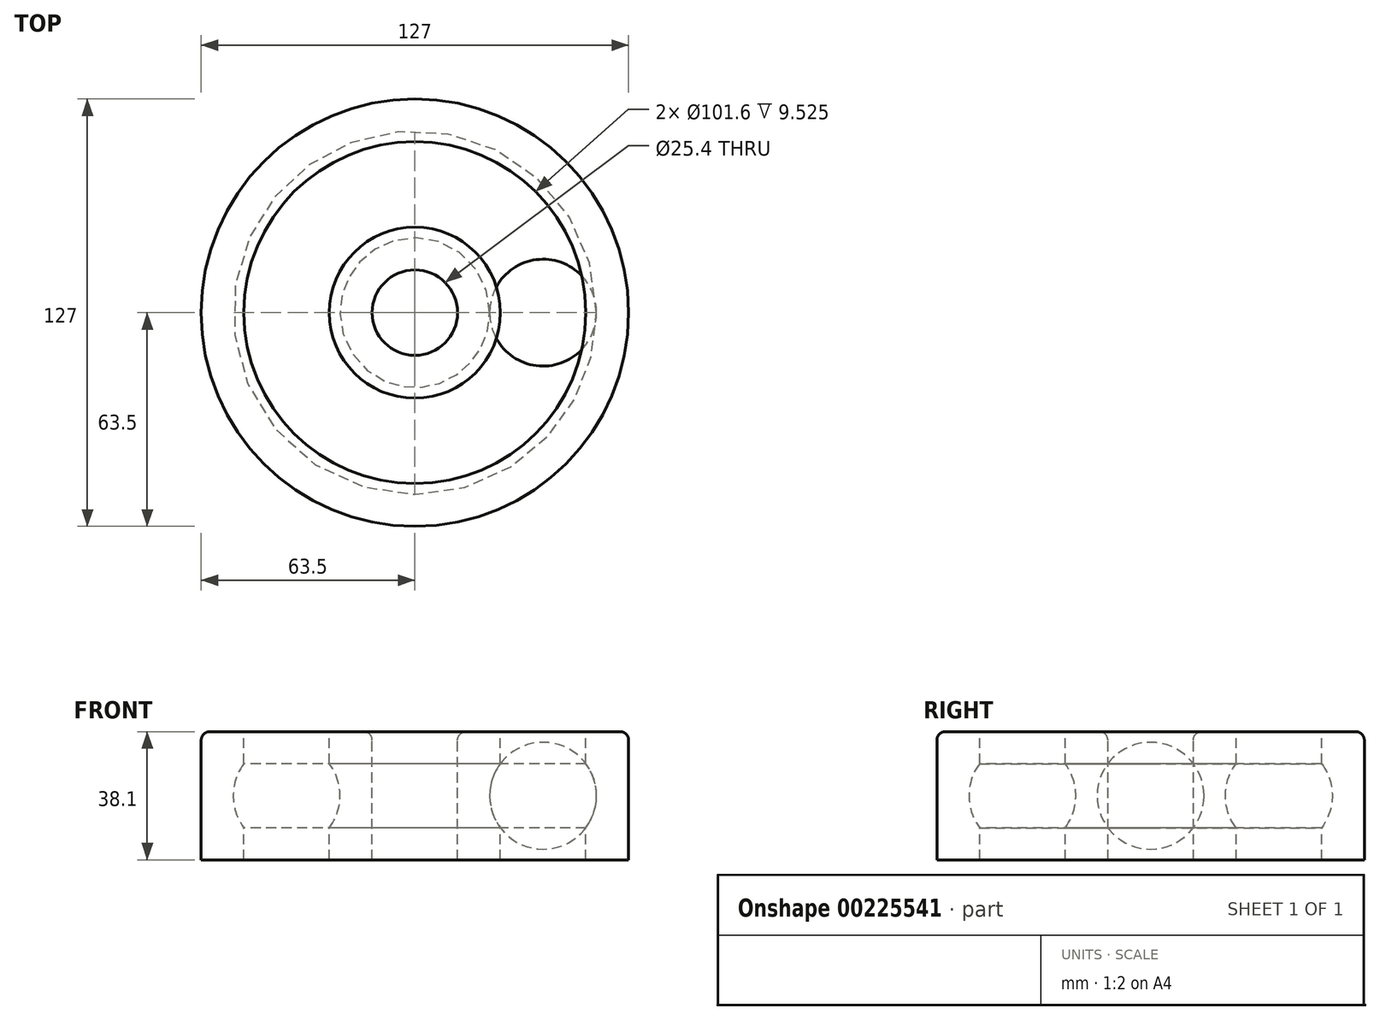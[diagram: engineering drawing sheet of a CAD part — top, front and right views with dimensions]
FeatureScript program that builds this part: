
annotation { "Feature Type Name" : "Feature", "Feature Type Description" : "" }
export const myFeature = defineFeature(function(context is Context, id is Id, definition is map)
    precondition{}
    {
        {
            var Q0;
            Q0=qCreatedBy(makeId("Front.planeOp"),FACE);
            var sketch = newSketch(context, id + "F0", { "sketchPlane" : qUnion([Q0])});
            skLineSegment(sketch, "E0", {"start": v(0, 19.05) * mm, "end": v(0, -19.05) * mm, "construction": true});
            skLineSegment(sketch, "E1", {"start": v(12.7, 19.05) * mm, "end": v(12.7, -19.05) * mm});
            skLineSegment(sketch, "E2", {"start": v(12.7, -19.05) * mm, "end": v(25.4, -19.05) * mm});
            skLineSegment(sketch, "E3", {"start": v(25.4, -19.05) * mm, "end": v(25.4, 19.05) * mm});
            skLineSegment(sketch, "E4", {"start": v(25.4, 19.05) * mm, "end": v(12.7, 19.05) * mm});
            skCircle(sketch, "E5", {"center": v(38.1, 0) * mm, "radius": 15.88 * mm});
            skLineSegment(sketch, "E6.bottom", {"start": v(50.8, 19.05) * mm, "end": v(63.5, 19.05) * mm});
            skLineSegment(sketch, "E6.top", {"start": v(50.8, -19.05) * mm, "end": v(63.5, -19.05) * mm});
            skLineSegment(sketch, "E6.left", {"start": v(50.8, 19.05) * mm, "end": v(50.8, -19.05) * mm});
            skLineSegment(sketch, "E6.right", {"start": v(63.5, 19.05) * mm, "end": v(63.5, -19.05) * mm});
            skLineSegment(sketch, "E7", {"start": v(22.22, 0) * mm, "end": v(53.97, 0) * mm});
            skLineSegment(sketch, "E8", {"start": v(12.7, 0) * mm, "end": v(22.22, 0) * mm, "construction": true});
            skLineSegment(sketch, "E9", {"start": v(53.97, 0) * mm, "end": v(63.5, 0) * mm, "construction": true});
            skSolve(sketch);
        }
        {
            var Q0;
            {var subQ6=sQuery(id+"F0.wireOp",EDGE,"E6.bottom");Q0=makeQuery(id+"F0.imprint","IMPRINT",FACE,{"disambiguationData":[TD([[makeQuery(id+"F0.imprint","IMPRINT",EDGE,{"derivedFrom":subQ6}),-1.0]])]});}
            var Q1;
            Q1=makeQuery(id+"F0.imprint","IMPRINT",FACE,{"disambiguationData":[TD([[makeQuery(id+"F0.imprint","IMPRINT",EDGE,{"derivedFrom":sQuery(id+"F0.wireOp",EDGE,"E1")}),1.0]])]});
            var Q2;
            Q2=sQuery(id+"F0.wireOp",EDGE,"E0");
            revolve(context, id + "F1", {"entities" : qUnion([Q0, Q1]), "axis" : qUnion([Q2]), "revolveType" : RevolveType.FULL});
        }
        {
            var Q0;
            Q0=qCreatedBy(makeId("Front.planeOp"),FACE);
            var sketch = newSketch(context, id + "F2", { "sketchPlane" : qUnion([Q0])});
            skCircle(sketch, "E10.0", {"center": v(38.1, 0) * mm, "radius": 15.88 * mm});
            skSolve(sketch);
        }
        {
            var Q0;
            {var subQ0=sQuery(id+"F0.wireOp",EDGE,"E5");var subQ1=sQuery(id+"F0.wireOp",EDGE,"E3");var subQ2=makeQuery(id+"F0.imprint","INTERSECT",VERTEX,{"disambiguationData":[OD(0.0)],"derivedFrom":[subQ1,subQ0]});Q0=makeQuery(id+"F0.imprint","IMPRINT",FACE,{"disambiguationData":[TD([[makeQuery(id+"F0.imprint","IMPRINT",EDGE,{"disambiguationData":[TD([[subQ2,-1.0]])],"derivedFrom":subQ1}),-1.0]])]});}
            var sketch = newSketch(context, id + "F3", { "sketchPlane" : qUnion([Q0])});
            skArc(sketch, "E11.0", {"start": v(53.97, 0) * mm, "mid": v(38.1, 15.88) * mm, "end": v(22.22, 0) * mm});
            skLineSegment(sketch, "E12.0", {"start": v(22.22, 0) * mm, "end": v(53.97, 0) * mm});
            skLineSegment(sketch, "E13.1", {"start": v(12.7, 0) * mm, "end": v(22.22, 0) * mm});
            skLineSegment(sketch, "E13.2", {"start": v(53.97, 0) * mm, "end": v(63.5, 0) * mm});
            skSolve(sketch);
        }
        {
            var Q0;
            {var subQ0=sQuery(id+"F3.wireOp",EDGE,"E11.0");Q0=makeQuery(id+"F3.imprint","IMPRINT",FACE,{"disambiguationData":[TD([[makeQuery(id+"F3.imprint","IMPRINT",EDGE,{"derivedFrom":subQ0}),1.0]])]});}
            var Q1;
            Q1=sQuery(id+"F3.wireOp",EDGE,"E12.0");
            revolve(context, id + "F4", {"entities" : qUnion([Q0]), "axis" : qUnion([Q1]), "revolveType" : RevolveType.FULL});
        }
        {
            var Q0;
            Q0=makeQuery(id+"F1.opRevolve","SWEPT_EDGE",EDGE,{"disambiguationData":[OSD([sQuery(id+"F0.wireOp",EDGE,"E6.bottom"),sQuery(id+"F0.wireOp",EDGE,"E6.right")])]});
            var Q1;
            Q1=makeQuery(id+"F1.opRevolve","SWEPT_EDGE",EDGE,{"disambiguationData":[OSD([sQuery(id+"F0.wireOp",EDGE,"E1"),sQuery(id+"F0.wireOp",EDGE,"E4")])]});
            fillet(context, id + "F5", {"entities" : qUnion([Q0, Q1]), "radius" : 2.54 * mm, "tangentPropagation" : true, "allowEdgeOverflow" : false});
        }
    });
